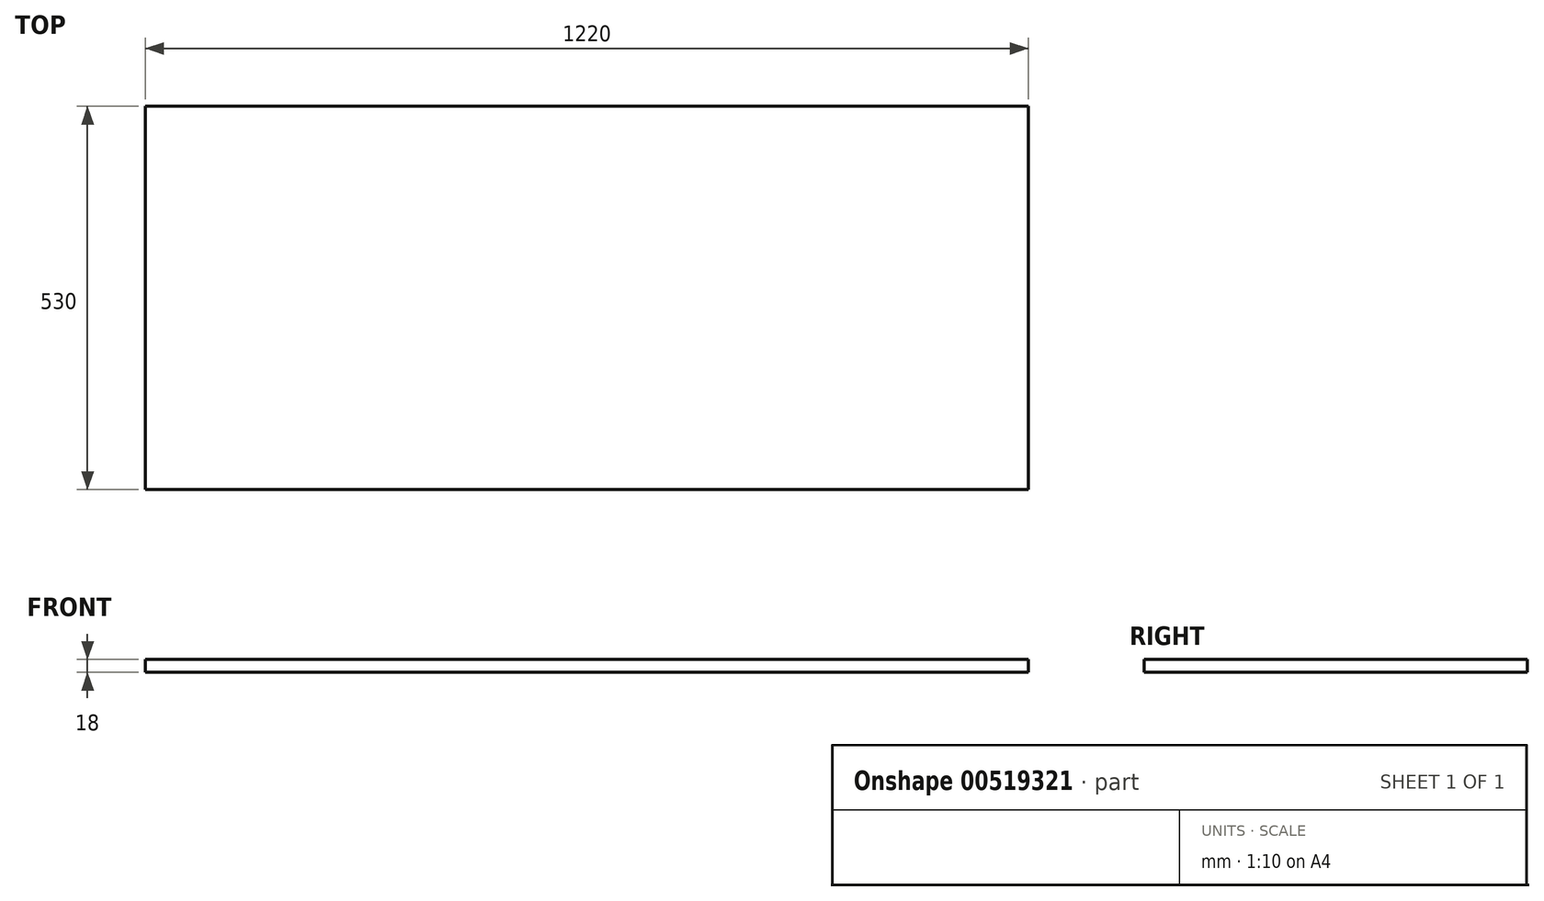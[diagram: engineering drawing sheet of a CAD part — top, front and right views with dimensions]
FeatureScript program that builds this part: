
annotation { "Feature Type Name" : "Feature", "Feature Type Description" : "" }
export const myFeature = defineFeature(function(context is Context, id is Id, definition is map)
    precondition{}
    {
        {
            var Q0;
            Q0=qCreatedBy(makeId("Top.planeOp"),FACE);
            var sketch = newSketch(context, id + "F0", { "sketchPlane" : qUnion([Q0])});
            skLineSegment(sketch, "E0.bottom", {"start": v(610, 265) * mm, "end": v(-610, 265) * mm});
            skLineSegment(sketch, "E0.top", {"start": v(610, -265) * mm, "end": v(-610, -265) * mm});
            skLineSegment(sketch, "E0.left", {"start": v(610, 265) * mm, "end": v(610, -265) * mm});
            skLineSegment(sketch, "E0.right", {"start": v(-610, 265) * mm, "end": v(-610, -265) * mm});
            skPoint(sketch, "E0.middle", {"position": v(0, 0) * mm});
            skSolve(sketch);
        }
        {
            var Q0;
            Q0 = qSketchRegion(id + "F0", true);
            extrude(context, id + "F1", {"entities" : qUnion([Q0]), "depth" : 18 * mm, "offsetDistance" : 25 * mm});
        }
    });
